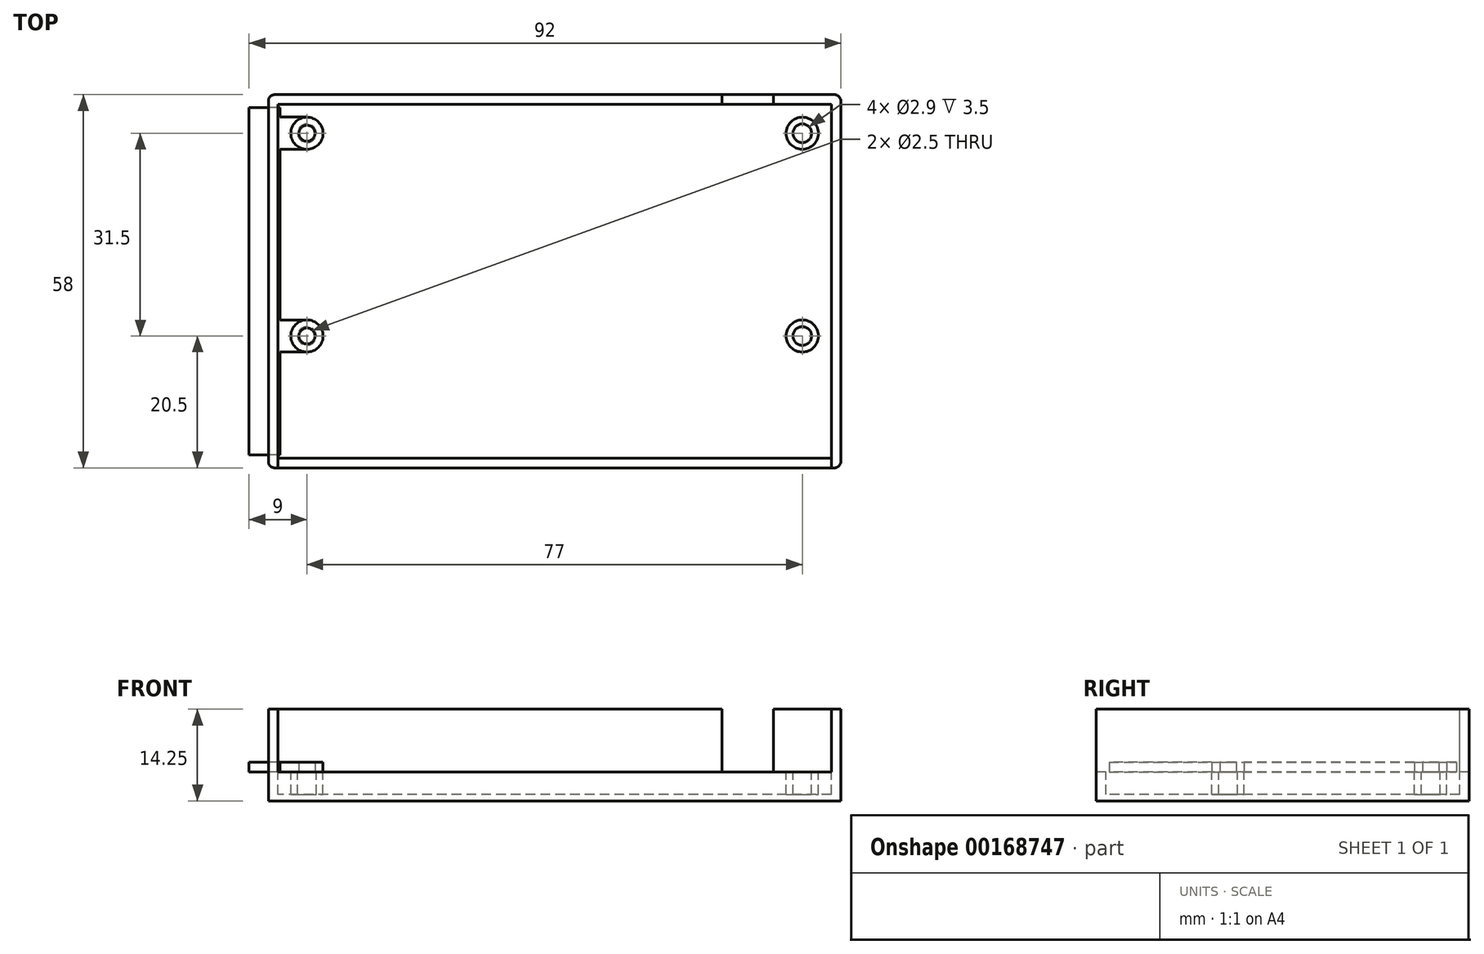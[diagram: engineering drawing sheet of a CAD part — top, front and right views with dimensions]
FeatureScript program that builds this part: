
annotation { "Feature Type Name" : "Feature", "Feature Type Description" : "" }
export const myFeature = defineFeature(function(context is Context, id is Id, definition is map)
    precondition{}
    {
        {
            var Q0;
            Q0=qCreatedBy(makeId("Top.planeOp"),FACE);
            var sketch = newSketch(context, id + "F11", { "sketchPlane" : qUnion([Q0])});
            skLineSegment(sketch, "E0.bottom", {"start": v(42.5, 27) * mm, "end": v(-42.5, 27) * mm});
            skLineSegment(sketch, "E0.top", {"start": v(42.5, -27) * mm, "end": v(-42.5, -27) * mm});
            skLineSegment(sketch, "E0.left", {"start": v(42.5, 27) * mm, "end": v(42.5, -27) * mm});
            skLineSegment(sketch, "E0.right", {"start": v(-42.5, 27) * mm, "end": v(-42.5, -27) * mm});
            skPoint(sketch, "E0.middle", {"position": v(0, 0) * mm});
            skCircle(sketch, "E1", {"center": v(-38.5, 23) * mm, "radius": 1.25 * mm, "construction": true});
            skCircle(sketch, "E2", {"center": v(38.5, 23) * mm, "radius": 1.25 * mm, "construction": true});
            skCircle(sketch, "E3", {"center": v(-38.5, -8.5) * mm, "radius": 1.25 * mm, "construction": true});
            skCircle(sketch, "E4", {"center": v(38.5, -8.5) * mm, "radius": 1.25 * mm, "construction": true});
            skPoint(sketch, "E5", {"position": v(-34.5, -27) * mm});
            skPoint(sketch, "E6", {"position": v(-17.5, -27) * mm});
            skPoint(sketch, "E7", {"position": v(-0.9, -27) * mm});
            skPoint(sketch, "E8", {"position": v(14.1, -27) * mm});
            skPoint(sketch, "E9", {"position": v(33.5, -27) * mm});
            skCircle(sketch, "E10", {"center": v(-38.5, 23) * mm, "radius": 2.5 * mm, "construction": true});
            skCircle(sketch, "E11", {"center": v(38.5, 23) * mm, "radius": 2.5 * mm, "construction": true});
            skCircle(sketch, "E12", {"center": v(38.5, -8.5) * mm, "radius": 2.5 * mm, "construction": true});
            skCircle(sketch, "E13", {"center": v(-38.5, -8.5) * mm, "radius": 2.5 * mm, "construction": true});
            skLineSegment(sketch, "E14.bottom", {"start": v(-41.5, -27) * mm, "end": v(-27.5, -27) * mm, "construction": true});
            skLineSegment(sketch, "E14.top", {"start": v(-41.5, -12) * mm, "end": v(-27.5, -12) * mm, "construction": true});
            skLineSegment(sketch, "E14.left", {"start": v(-41.5, -27) * mm, "end": v(-41.5, -12) * mm, "construction": true});
            skLineSegment(sketch, "E14.right", {"start": v(-27.5, -27) * mm, "end": v(-27.5, -12) * mm, "construction": true});
            skLineSegment(sketch, "E15.bottom", {"start": v(-25, -17) * mm, "end": v(-10, -17) * mm, "construction": true});
            skLineSegment(sketch, "E15.top", {"start": v(-25, -27) * mm, "end": v(-10, -27) * mm, "construction": true});
            skLineSegment(sketch, "E15.left", {"start": v(-25, -17) * mm, "end": v(-25, -27) * mm, "construction": true});
            skLineSegment(sketch, "E15.right", {"start": v(-10, -17) * mm, "end": v(-10, -27) * mm, "construction": true});
            skLineSegment(sketch, "E16.bottom", {"start": v(-4.9, -21) * mm, "end": v(3.1, -21) * mm, "construction": true});
            skLineSegment(sketch, "E16.top", {"start": v(-4.9, -27) * mm, "end": v(3.1, -27) * mm, "construction": true});
            skLineSegment(sketch, "E16.left", {"start": v(-4.9, -21) * mm, "end": v(-4.9, -27) * mm, "construction": true});
            skLineSegment(sketch, "E16.right", {"start": v(3.1, -21) * mm, "end": v(3.1, -27) * mm, "construction": true});
            skLineSegment(sketch, "E17.bottom", {"start": v(6.6, -13) * mm, "end": v(21.6, -13) * mm, "construction": true});
            skLineSegment(sketch, "E17.top", {"start": v(6.6, -27) * mm, "end": v(21.6, -27) * mm, "construction": true});
            skLineSegment(sketch, "E17.left", {"start": v(6.6, -13) * mm, "end": v(6.6, -27) * mm, "construction": true});
            skLineSegment(sketch, "E17.right", {"start": v(21.6, -13) * mm, "end": v(21.6, -27) * mm, "construction": true});
            skLineSegment(sketch, "E18.bottom", {"start": v(26, -13) * mm, "end": v(41, -13) * mm, "construction": true});
            skLineSegment(sketch, "E18.top", {"start": v(26, -27) * mm, "end": v(41, -27) * mm, "construction": true});
            skLineSegment(sketch, "E18.left", {"start": v(26, -13) * mm, "end": v(26, -27) * mm, "construction": true});
            skLineSegment(sketch, "E18.right", {"start": v(41, -13) * mm, "end": v(41, -27) * mm, "construction": true});
            skPoint(sketch, "E19", {"position": v(30, 27) * mm});
            skLineSegment(sketch, "E20.bottom", {"start": v(26, 27) * mm, "end": v(34, 27) * mm, "construction": true});
            skLineSegment(sketch, "E20.top", {"start": v(26, 14) * mm, "end": v(34, 14) * mm, "construction": true});
            skLineSegment(sketch, "E20.left", {"start": v(26, 27) * mm, "end": v(26, 14) * mm, "construction": true});
            skLineSegment(sketch, "E20.right", {"start": v(34, 27) * mm, "end": v(34, 14) * mm, "construction": true});
            skLineSegment(sketch, "E21.bottom", {"start": v(-31.5, 21) * mm, "end": v(-33.5, 21) * mm, "construction": true});
            skLineSegment(sketch, "E21.top", {"start": v(-31.5, 25) * mm, "end": v(-33.5, 25) * mm, "construction": true});
            skLineSegment(sketch, "E21.left", {"start": v(-31.5, 21) * mm, "end": v(-31.5, 25) * mm, "construction": true});
            skLineSegment(sketch, "E21.right", {"start": v(-33.5, 21) * mm, "end": v(-33.5, 25) * mm, "construction": true});
            skPoint(sketch, "E21.middle", {"position": v(-32.5, 23) * mm});
            skLineSegment(sketch, "E22", {"start": v(-32.5, 24) * mm, "end": v(-32.5, 22) * mm, "construction": true});
            skPoint(sketch, "E23.1.0.0", {"position": v(-30.5, 23) * mm});
            skLineSegment(sketch, "E23.1.0.2", {"start": v(-29.5, 21) * mm, "end": v(-29.5, 25) * mm, "construction": true});
            skLineSegment(sketch, "E23.1.0.3", {"start": v(-29.5, 25) * mm, "end": v(-31.5, 25) * mm, "construction": true});
            skLineSegment(sketch, "E23.1.0.4", {"start": v(-29.5, 21) * mm, "end": v(-31.5, 21) * mm, "construction": true});
            skLineSegment(sketch, "E23.1.0.5", {"start": v(-30.5, 24) * mm, "end": v(-30.5, 22) * mm, "construction": true});
            skPoint(sketch, "E23.2.0.0", {"position": v(-28.5, 23) * mm});
            skLineSegment(sketch, "E23.2.0.1", {"start": v(-29.5, 21) * mm, "end": v(-29.5, 25) * mm, "construction": true});
            skLineSegment(sketch, "E23.2.0.2", {"start": v(-27.5, 21) * mm, "end": v(-27.5, 25) * mm, "construction": true});
            skLineSegment(sketch, "E23.2.0.3", {"start": v(-27.5, 25) * mm, "end": v(-29.5, 25) * mm, "construction": true});
            skLineSegment(sketch, "E23.2.0.4", {"start": v(-27.5, 21) * mm, "end": v(-29.5, 21) * mm, "construction": true});
            skLineSegment(sketch, "E23.2.0.5", {"start": v(-28.5, 24) * mm, "end": v(-28.5, 22) * mm, "construction": true});
            skPoint(sketch, "E23.3.0.0", {"position": v(-26.5, 23) * mm});
            skLineSegment(sketch, "E23.3.0.1", {"start": v(-27.5, 21) * mm, "end": v(-27.5, 25) * mm, "construction": true});
            skLineSegment(sketch, "E23.3.0.2", {"start": v(-25.5, 21) * mm, "end": v(-25.5, 25) * mm, "construction": true});
            skLineSegment(sketch, "E23.3.0.3", {"start": v(-25.5, 25) * mm, "end": v(-27.5, 25) * mm, "construction": true});
            skLineSegment(sketch, "E23.3.0.4", {"start": v(-25.5, 21) * mm, "end": v(-27.5, 21) * mm, "construction": true});
            skLineSegment(sketch, "E23.3.0.5", {"start": v(-26.5, 24) * mm, "end": v(-26.5, 22) * mm, "construction": true});
            skPoint(sketch, "E23.4.0.0", {"position": v(-24.5, 23) * mm});
            skLineSegment(sketch, "E23.4.0.1", {"start": v(-25.5, 21) * mm, "end": v(-25.5, 25) * mm, "construction": true});
            skLineSegment(sketch, "E23.4.0.2", {"start": v(-23.5, 21) * mm, "end": v(-23.5, 25) * mm, "construction": true});
            skLineSegment(sketch, "E23.4.0.3", {"start": v(-23.5, 25) * mm, "end": v(-25.5, 25) * mm, "construction": true});
            skLineSegment(sketch, "E23.4.0.4", {"start": v(-23.5, 21) * mm, "end": v(-25.5, 21) * mm, "construction": true});
            skLineSegment(sketch, "E23.4.0.5", {"start": v(-24.5, 24) * mm, "end": v(-24.5, 22) * mm, "construction": true});
            skPoint(sketch, "E23.5.0.0", {"position": v(-22.5, 23) * mm});
            skLineSegment(sketch, "E23.5.0.1", {"start": v(-23.5, 21) * mm, "end": v(-23.5, 25) * mm, "construction": true});
            skLineSegment(sketch, "E23.5.0.2", {"start": v(-21.5, 21) * mm, "end": v(-21.5, 25) * mm, "construction": true});
            skLineSegment(sketch, "E23.5.0.3", {"start": v(-21.5, 25) * mm, "end": v(-23.5, 25) * mm, "construction": true});
            skLineSegment(sketch, "E23.5.0.4", {"start": v(-21.5, 21) * mm, "end": v(-23.5, 21) * mm, "construction": true});
            skLineSegment(sketch, "E23.5.0.5", {"start": v(-22.5, 24) * mm, "end": v(-22.5, 22) * mm, "construction": true});
            skPoint(sketch, "E23.6.0.0", {"position": v(-20.5, 23) * mm});
            skLineSegment(sketch, "E23.6.0.1", {"start": v(-21.5, 21) * mm, "end": v(-21.5, 25) * mm, "construction": true});
            skLineSegment(sketch, "E23.6.0.2", {"start": v(-19.5, 21) * mm, "end": v(-19.5, 25) * mm, "construction": true});
            skLineSegment(sketch, "E23.6.0.3", {"start": v(-19.5, 25) * mm, "end": v(-21.5, 25) * mm, "construction": true});
            skLineSegment(sketch, "E23.6.0.4", {"start": v(-19.5, 21) * mm, "end": v(-21.5, 21) * mm, "construction": true});
            skLineSegment(sketch, "E23.6.0.5", {"start": v(-20.5, 24) * mm, "end": v(-20.5, 22) * mm, "construction": true});
            skPoint(sketch, "E23.7.0.0", {"position": v(-18.5, 23) * mm});
            skLineSegment(sketch, "E23.7.0.1", {"start": v(-19.5, 21) * mm, "end": v(-19.5, 25) * mm, "construction": true});
            skLineSegment(sketch, "E23.7.0.2", {"start": v(-17.5, 21) * mm, "end": v(-17.5, 25) * mm, "construction": true});
            skLineSegment(sketch, "E23.7.0.3", {"start": v(-17.5, 25) * mm, "end": v(-19.5, 25) * mm, "construction": true});
            skLineSegment(sketch, "E23.7.0.4", {"start": v(-17.5, 21) * mm, "end": v(-19.5, 21) * mm, "construction": true});
            skLineSegment(sketch, "E23.7.0.5", {"start": v(-18.5, 24) * mm, "end": v(-18.5, 22) * mm, "construction": true});
            skPoint(sketch, "E23.8.0.0", {"position": v(-16.5, 23) * mm});
            skLineSegment(sketch, "E23.8.0.1", {"start": v(-17.5, 21) * mm, "end": v(-17.5, 25) * mm, "construction": true});
            skLineSegment(sketch, "E23.8.0.2", {"start": v(-15.5, 21) * mm, "end": v(-15.5, 25) * mm, "construction": true});
            skLineSegment(sketch, "E23.8.0.3", {"start": v(-15.5, 25) * mm, "end": v(-17.5, 25) * mm, "construction": true});
            skLineSegment(sketch, "E23.8.0.4", {"start": v(-15.5, 21) * mm, "end": v(-17.5, 21) * mm, "construction": true});
            skLineSegment(sketch, "E23.8.0.5", {"start": v(-16.5, 24) * mm, "end": v(-16.5, 22) * mm, "construction": true});
            skPoint(sketch, "E23.9.0.0", {"position": v(-14.5, 23) * mm});
            skLineSegment(sketch, "E23.9.0.1", {"start": v(-15.5, 21) * mm, "end": v(-15.5, 25) * mm, "construction": true});
            skLineSegment(sketch, "E23.9.0.2", {"start": v(-13.5, 21) * mm, "end": v(-13.5, 25) * mm, "construction": true});
            skLineSegment(sketch, "E23.9.0.3", {"start": v(-13.5, 25) * mm, "end": v(-15.5, 25) * mm, "construction": true});
            skLineSegment(sketch, "E23.9.0.4", {"start": v(-13.5, 21) * mm, "end": v(-15.5, 21) * mm, "construction": true});
            skLineSegment(sketch, "E23.9.0.5", {"start": v(-14.5, 24) * mm, "end": v(-14.5, 22) * mm, "construction": true});
            skPoint(sketch, "E23.10.0.0", {"position": v(-12.5, 23) * mm});
            skLineSegment(sketch, "E23.10.0.1", {"start": v(-13.5, 21) * mm, "end": v(-13.5, 25) * mm, "construction": true});
            skLineSegment(sketch, "E23.10.0.2", {"start": v(-11.5, 21) * mm, "end": v(-11.5, 25) * mm, "construction": true});
            skLineSegment(sketch, "E23.10.0.3", {"start": v(-11.5, 25) * mm, "end": v(-13.5, 25) * mm, "construction": true});
            skLineSegment(sketch, "E23.10.0.4", {"start": v(-11.5, 21) * mm, "end": v(-13.5, 21) * mm, "construction": true});
            skLineSegment(sketch, "E23.10.0.5", {"start": v(-12.5, 24) * mm, "end": v(-12.5, 22) * mm, "construction": true});
            skPoint(sketch, "E23.11.0.0", {"position": v(-10.5, 23) * mm});
            skLineSegment(sketch, "E23.11.0.1", {"start": v(-11.5, 21) * mm, "end": v(-11.5, 25) * mm, "construction": true});
            skLineSegment(sketch, "E23.11.0.2", {"start": v(-9.5, 21) * mm, "end": v(-9.5, 25) * mm, "construction": true});
            skLineSegment(sketch, "E23.11.0.3", {"start": v(-9.5, 25) * mm, "end": v(-11.5, 25) * mm, "construction": true});
            skLineSegment(sketch, "E23.11.0.4", {"start": v(-9.5, 21) * mm, "end": v(-11.5, 21) * mm, "construction": true});
            skLineSegment(sketch, "E23.11.0.5", {"start": v(-10.5, 24) * mm, "end": v(-10.5, 22) * mm, "construction": true});
            skPoint(sketch, "E23.12.0.0", {"position": v(-8.5, 23) * mm});
            skLineSegment(sketch, "E23.12.0.1", {"start": v(-9.5, 21) * mm, "end": v(-9.5, 25) * mm, "construction": true});
            skLineSegment(sketch, "E23.12.0.2", {"start": v(-7.5, 21) * mm, "end": v(-7.5, 25) * mm, "construction": true});
            skLineSegment(sketch, "E23.12.0.3", {"start": v(-7.5, 25) * mm, "end": v(-9.5, 25) * mm, "construction": true});
            skLineSegment(sketch, "E23.12.0.4", {"start": v(-7.5, 21) * mm, "end": v(-9.5, 21) * mm, "construction": true});
            skLineSegment(sketch, "E23.12.0.5", {"start": v(-8.5, 24) * mm, "end": v(-8.5, 22) * mm, "construction": true});
            skPoint(sketch, "E23.13.0.0", {"position": v(-6.5, 23) * mm});
            skLineSegment(sketch, "E23.13.0.1", {"start": v(-7.5, 21) * mm, "end": v(-7.5, 25) * mm, "construction": true});
            skLineSegment(sketch, "E23.13.0.2", {"start": v(-5.5, 21) * mm, "end": v(-5.5, 25) * mm, "construction": true});
            skLineSegment(sketch, "E23.13.0.3", {"start": v(-5.5, 25) * mm, "end": v(-7.5, 25) * mm, "construction": true});
            skLineSegment(sketch, "E23.13.0.4", {"start": v(-5.5, 21) * mm, "end": v(-7.5, 21) * mm, "construction": true});
            skLineSegment(sketch, "E23.13.0.5", {"start": v(-6.5, 24) * mm, "end": v(-6.5, 22) * mm, "construction": true});
            skPoint(sketch, "E23.14.0.0", {"position": v(-4.5, 23) * mm});
            skLineSegment(sketch, "E23.14.0.1", {"start": v(-5.5, 21) * mm, "end": v(-5.5, 25) * mm, "construction": true});
            skLineSegment(sketch, "E23.14.0.2", {"start": v(-3.5, 21) * mm, "end": v(-3.5, 25) * mm, "construction": true});
            skLineSegment(sketch, "E23.14.0.3", {"start": v(-3.5, 25) * mm, "end": v(-5.5, 25) * mm, "construction": true});
            skLineSegment(sketch, "E23.14.0.4", {"start": v(-3.5, 21) * mm, "end": v(-5.5, 21) * mm, "construction": true});
            skLineSegment(sketch, "E23.14.0.5", {"start": v(-4.5, 24) * mm, "end": v(-4.5, 22) * mm, "construction": true});
            skPoint(sketch, "E23.15.0.0", {"position": v(-2.5, 23) * mm});
            skLineSegment(sketch, "E23.15.0.1", {"start": v(-3.5, 21) * mm, "end": v(-3.5, 25) * mm, "construction": true});
            skLineSegment(sketch, "E23.15.0.2", {"start": v(-1.5, 21) * mm, "end": v(-1.5, 25) * mm, "construction": true});
            skLineSegment(sketch, "E23.15.0.3", {"start": v(-1.5, 25) * mm, "end": v(-3.5, 25) * mm, "construction": true});
            skLineSegment(sketch, "E23.15.0.4", {"start": v(-1.5, 21) * mm, "end": v(-3.5, 21) * mm, "construction": true});
            skLineSegment(sketch, "E23.15.0.5", {"start": v(-2.5, 24) * mm, "end": v(-2.5, 22) * mm, "construction": true});
            skPoint(sketch, "E23.16.0.0", {"position": v(-0.5, 23) * mm});
            skLineSegment(sketch, "E23.16.0.1", {"start": v(-1.5, 21) * mm, "end": v(-1.5, 25) * mm, "construction": true});
            skLineSegment(sketch, "E23.16.0.2", {"start": v(0.5, 21) * mm, "end": v(0.5, 25) * mm, "construction": true});
            skLineSegment(sketch, "E23.16.0.3", {"start": v(0.5, 25) * mm, "end": v(-1.5, 25) * mm, "construction": true});
            skLineSegment(sketch, "E23.16.0.4", {"start": v(0.5, 21) * mm, "end": v(-1.5, 21) * mm, "construction": true});
            skLineSegment(sketch, "E23.16.0.5", {"start": v(-0.5, 24) * mm, "end": v(-0.5, 22) * mm, "construction": true});
            skPoint(sketch, "E23.17.0.0", {"position": v(1.5, 23) * mm});
            skLineSegment(sketch, "E23.17.0.1", {"start": v(0.5, 21) * mm, "end": v(0.5, 25) * mm, "construction": true});
            skLineSegment(sketch, "E23.17.0.2", {"start": v(2.5, 21) * mm, "end": v(2.5, 25) * mm, "construction": true});
            skLineSegment(sketch, "E23.17.0.3", {"start": v(2.5, 25) * mm, "end": v(0.5, 25) * mm, "construction": true});
            skLineSegment(sketch, "E23.17.0.4", {"start": v(2.5, 21) * mm, "end": v(0.5, 21) * mm, "construction": true});
            skLineSegment(sketch, "E23.17.0.5", {"start": v(1.5, 24) * mm, "end": v(1.5, 22) * mm, "construction": true});
            skPoint(sketch, "E23.18.0.0", {"position": v(3.5, 23) * mm});
            skLineSegment(sketch, "E23.18.0.1", {"start": v(2.5, 21) * mm, "end": v(2.5, 25) * mm, "construction": true});
            skLineSegment(sketch, "E23.18.0.2", {"start": v(4.5, 21) * mm, "end": v(4.5, 25) * mm, "construction": true});
            skLineSegment(sketch, "E23.18.0.3", {"start": v(4.5, 25) * mm, "end": v(2.5, 25) * mm, "construction": true});
            skLineSegment(sketch, "E23.18.0.4", {"start": v(4.5, 21) * mm, "end": v(2.5, 21) * mm, "construction": true});
            skLineSegment(sketch, "E23.18.0.5", {"start": v(3.5, 24) * mm, "end": v(3.5, 22) * mm, "construction": true});
            skPoint(sketch, "E23.19.0.0", {"position": v(5.5, 23) * mm});
            skLineSegment(sketch, "E23.19.0.1", {"start": v(4.5, 21) * mm, "end": v(4.5, 25) * mm, "construction": true});
            skLineSegment(sketch, "E23.19.0.2", {"start": v(6.5, 21) * mm, "end": v(6.5, 25) * mm, "construction": true});
            skLineSegment(sketch, "E23.19.0.3", {"start": v(6.5, 25) * mm, "end": v(4.5, 25) * mm, "construction": true});
            skLineSegment(sketch, "E23.19.0.4", {"start": v(6.5, 21) * mm, "end": v(4.5, 21) * mm, "construction": true});
            skLineSegment(sketch, "E23.19.0.5", {"start": v(5.5, 24) * mm, "end": v(5.5, 22) * mm, "construction": true});
            skLineSegment(sketch, "E23.direction1", {"start": v(-33.5, 21) * mm, "end": v(-31.5, 21) * mm, "construction": true});
            skLineSegment(sketch, "E24.bottom", {"start": v(8, 19.75) * mm, "end": v(-35, 19.75) * mm, "construction": true});
            skLineSegment(sketch, "E24.top", {"start": v(8, 26.25) * mm, "end": v(-35, 26.25) * mm, "construction": true});
            skLineSegment(sketch, "E24.left", {"start": v(8, 19.75) * mm, "end": v(8, 26.25) * mm, "construction": true});
            skLineSegment(sketch, "E24.right", {"start": v(-35, 19.75) * mm, "end": v(-35, 26.25) * mm, "construction": true});
            skPoint(sketch, "E24.middle", {"position": v(-13.5, 23) * mm});
            skSolve(sketch);
        }
        {
            var Q0;
            Q0=qCreatedBy(makeId("Front.planeOp"),FACE);
            var sketch = newSketch(context, id + "F0", { "sketchPlane" : qUnion([Q0])});
            skLineSegment(sketch, "E25", {"start": v(0, 0) * mm, "end": v(0, -3.5) * mm});
            skLineSegment(sketch, "E26", {"start": v(0, 0) * mm, "end": v(0, 1.25) * mm});
            skLineSegment(sketch, "E27", {"start": v(0, 1.25) * mm, "end": v(0, 9.75) * mm});
            skSolve(sketch);
        }
        {
            var Q0;
            Q0=sQuery(id+"F0.wireOp",VERTEX,"E25.end");
            var Q1;
            Q1=sQuery(id+"F0.wireOp",EDGE,"E25");
            cPlane(context, id + "F1", {"entities" : qUnion([Q0, Q1]), "cplaneType" : CPlaneType.LINE_POINT, "offset" : 25 * mm, "width" : 150 * mm, "height" : 150 * mm});
        }
        {
            var Q0;
            Q0=qCreatedBy(id+"F1.planeOp",FACE);
            var sketch = newSketch(context, id + "F2", { "sketchPlane" : qUnion([Q0])});
            skLineSegment(sketch, "E28.0", {"start": v(43, -27.5) * mm, "end": v(-43, -27.5) * mm});
            skLineSegment(sketch, "E28.1", {"start": v(43, -27.5) * mm, "end": v(43, 27.5) * mm});
            skLineSegment(sketch, "E28.2", {"start": v(43, 27.5) * mm, "end": v(-43, 27.5) * mm});
            skLineSegment(sketch, "E28.3", {"start": v(-43, -27.5) * mm, "end": v(-43, 27.5) * mm});
            skLineSegment(sketch, "E29.bottom", {"start": v(44.5, -29) * mm, "end": v(-44.5, -29) * mm});
            skLineSegment(sketch, "E29.top", {"start": v(44.5, 29) * mm, "end": v(-44.5, 29) * mm});
            skLineSegment(sketch, "E29.left", {"start": v(44.5, -29) * mm, "end": v(44.5, 29) * mm});
            skLineSegment(sketch, "E29.right", {"start": v(-44.5, -29) * mm, "end": v(-44.5, 29) * mm});
            skPoint(sketch, "E29.middle", {"position": v(0, 0) * mm});
            skLineSegment(sketch, "E30", {"start": v(-43, 27.5) * mm, "end": v(-43, 29) * mm});
            skLineSegment(sketch, "E31", {"start": v(43, 27.5) * mm, "end": v(43, 29) * mm});
            skLineSegment(sketch, "E32.0", {"start": v(26, -27) * mm, "end": v(34, -27) * mm, "construction": true});
            skLineSegment(sketch, "E33", {"start": v(26, -29) * mm, "end": v(26, -27.5) * mm});
            skLineSegment(sketch, "E34", {"start": v(34, -29) * mm, "end": v(34, -27.5) * mm});
            skSolve(sketch);
        }
        {
            var Q0;
            Q0=makeQuery(id+"F2.imprint","IMPRINT",FACE,{"disambiguationData":[TD([[makeQuery(id+"F2.imprint","IMPRINT",EDGE,{"derivedFrom":sQuery(id+"F2.wireOp",EDGE,"E28.0")}),-1.0]])]});
            var Q1;
            Q1=makeQuery(id+"F2.imprint","IMPRINT",FACE,{"disambiguationData":[TD([[makeQuery(id+"F2.imprint","IMPRINT",EDGE,{"derivedFrom":sQuery(id+"F2.wireOp",EDGE,"E28.2")}),-1.0]])]});
            var Q2;
            {var subQ5=sQuery(id+"F2.wireOp",EDGE,"E28.3");Q2=makeQuery(id+"F2.imprint","IMPRINT",FACE,{"disambiguationData":[TD([[makeQuery(id+"F2.imprint","IMPRINT",EDGE,{"derivedFrom":subQ5}),1.0]])]});}
            var Q3;
            {var subQ0=sQuery(id+"F2.wireOp",EDGE,"E33");Q3=makeQuery(id+"F2.imprint","IMPRINT",FACE,{"disambiguationData":[TD([[makeQuery(id+"F2.imprint","IMPRINT",EDGE,{"derivedFrom":subQ0}),-1.0]])]});}
            var Q4;
            {var subQ5=sQuery(id+"F2.wireOp",EDGE,"E28.1");Q4=makeQuery(id+"F2.imprint","IMPRINT",FACE,{"disambiguationData":[TD([[makeQuery(id+"F2.imprint","IMPRINT",EDGE,{"derivedFrom":subQ5}),-1.0]])]});}
            extrude(context, id + "F3", {"entities" : qUnion([Q0, Q1, Q2, Q3, Q4]), "depth" : 1 * mm});
        }
        {
            var Q0;
            {var subQ5=sQuery(id+"F2.wireOp",EDGE,"E28.3");Q0=makeQuery(id+"F2.imprint","IMPRINT",FACE,{"disambiguationData":[TD([[makeQuery(id+"F2.imprint","IMPRINT",EDGE,{"derivedFrom":subQ5}),1.0]])]});}
            var Q1;
            {var subQ5=sQuery(id+"F2.wireOp",EDGE,"E28.1");Q1=makeQuery(id+"F2.imprint","IMPRINT",FACE,{"disambiguationData":[TD([[makeQuery(id+"F2.imprint","IMPRINT",EDGE,{"derivedFrom":subQ5}),-1.0]])]});}
            var Q2;
            Q2=sQuery(id+"F0.wireOp",EDGE,"E25");
            var Q3;
            Q3=sQuery(id+"F0.wireOp",EDGE,"E26");
            var Q4;
            Q4=sQuery(id+"F0.wireOp",EDGE,"E27");
            sweep(context, id + "F4", {"operationType" : NewBodyOperationType.ADD, "profiles" : qUnion([Q0, Q1]), "path" : qUnion([Q2, Q3, Q4])});
        }
        {
            var Q0;
            Q0=qCreatedBy(id+"F1.planeOp",FACE);
            var sketch = newSketch(context, id + "F5", { "sketchPlane" : qUnion([Q0])});
            skCircle(sketch, "E35.0", {"center": v(-38.5, -23) * mm, "radius": 2.5 * mm});
            skCircle(sketch, "E36.0", {"center": v(-38.5, -23) * mm, "radius": 1.25 * mm, "construction": true});
            skCircle(sketch, "E37.0", {"center": v(-38.5, 8.5) * mm, "radius": 2.5 * mm});
            skCircle(sketch, "E38.0", {"center": v(-38.5, 8.5) * mm, "radius": 1.25 * mm, "construction": true});
            skCircle(sketch, "E39.0", {"center": v(38.5, 8.5) * mm, "radius": 2.5 * mm});
            skCircle(sketch, "E40.0", {"center": v(38.5, 8.5) * mm, "radius": 1.25 * mm, "construction": true});
            skCircle(sketch, "E41.0", {"center": v(38.5, -23) * mm, "radius": 2.5 * mm});
            skCircle(sketch, "E42.0", {"center": v(38.5, -23) * mm, "radius": 1.25 * mm, "construction": true});
            skCircle(sketch, "E43.0", {"center": v(-38.5, -23) * mm, "radius": 1.45 * mm});
            skCircle(sketch, "E44", {"center": v(38.5, -23) * mm, "radius": 1.45 * mm});
            skCircle(sketch, "E45", {"center": v(-38.5, 8.5) * mm, "radius": 1.45 * mm});
            skCircle(sketch, "E46", {"center": v(38.5, 8.5) * mm, "radius": 1.45 * mm});
            skSolve(sketch);
        }
        {
            var Q0;
            Q0 = qSketchRegion(id + "F5", true);
            var Q1;
            Q1=sQuery(id+"F0.wireOp",EDGE,"E25");
            sweep(context, id + "F6", {"operationType" : NewBodyOperationType.ADD, "profiles" : qUnion([Q0]), "path" : qUnion([Q1])});
        }
        {
            var Q0;
            Q0=makeQuery(id+"F2.imprint","IMPRINT",FACE,{"disambiguationData":[TD([[makeQuery(id+"F2.imprint","IMPRINT",EDGE,{"derivedFrom":sQuery(id+"F2.wireOp",EDGE,"E28.2")}),-1.0]])]});
            var Q1;
            {var subQ0=sQuery(id+"F2.wireOp",EDGE,"E33");Q1=makeQuery(id+"F2.imprint","IMPRINT",FACE,{"disambiguationData":[TD([[makeQuery(id+"F2.imprint","IMPRINT",EDGE,{"derivedFrom":subQ0}),-1.0]])]});}
            var Q2;
            Q2=sQuery(id+"F0.wireOp",EDGE,"E25");
            sweep(context, id + "F7", {"operationType" : NewBodyOperationType.ADD, "profiles" : qUnion([Q0, Q1]), "path" : qUnion([Q2])});
        }
        {
            var Q0;
            {var subQ0=sQuery(id+"F2.wireOp",EDGE,"E29.left");var subQ1=sQuery(id+"F2.wireOp",EDGE,"E29.top");Q0=makeQuery(id+"F4.boolean.opBoolean","MERGE",EDGE,{"derivedFrom":[makeQuery(id+"F3.opExtrude","SWEPT_EDGE",EDGE,{"disambiguationData":[OSD([subQ1,subQ0])]}),makeQuery(id+"F4.opSweep","SWEPT_EDGE",EDGE,{"disambiguationData":[OSD([sQuery(id+"F0.wireOp",EDGE,"E25"),subQ1,subQ0])]})]});}
            var Q1;
            {var subQ0=sQuery(id+"F2.wireOp",EDGE,"E29.left");var subQ1=sQuery(id+"F2.wireOp",EDGE,"E29.bottom");Q1=makeQuery(id+"F4.boolean.opBoolean","MERGE",EDGE,{"derivedFrom":[makeQuery(id+"F3.opExtrude","SWEPT_EDGE",EDGE,{"disambiguationData":[OSD([subQ1,subQ0])]}),makeQuery(id+"F4.opSweep","SWEPT_EDGE",EDGE,{"disambiguationData":[OSD([sQuery(id+"F0.wireOp",EDGE,"E25"),subQ1,subQ0])]})]});}
            var Q2;
            {var subQ0=sQuery(id+"F2.wireOp",EDGE,"E29.right");var subQ1=sQuery(id+"F2.wireOp",EDGE,"E29.top");Q2=makeQuery(id+"F4.boolean.opBoolean","MERGE",EDGE,{"derivedFrom":[makeQuery(id+"F3.opExtrude","SWEPT_EDGE",EDGE,{"disambiguationData":[OSD([subQ1,subQ0])]}),makeQuery(id+"F4.opSweep","SWEPT_EDGE",EDGE,{"disambiguationData":[OSD([sQuery(id+"F0.wireOp",EDGE,"E25"),subQ1,subQ0])]})]});}
            var Q3;
            {var subQ0=sQuery(id+"F2.wireOp",EDGE,"E29.right");var subQ1=sQuery(id+"F2.wireOp",EDGE,"E29.bottom");Q3=makeQuery(id+"F4.boolean.opBoolean","MERGE",EDGE,{"derivedFrom":[makeQuery(id+"F3.opExtrude","SWEPT_EDGE",EDGE,{"disambiguationData":[OSD([subQ1,subQ0])]}),makeQuery(id+"F4.opSweep","SWEPT_EDGE",EDGE,{"disambiguationData":[OSD([sQuery(id+"F0.wireOp",EDGE,"E25"),subQ1,subQ0])]})]});}
            fillet(context, id + "F8", {"entities" : qUnion([Q0, Q1, Q2, Q3]), "radius" : 1 * mm, "allowEdgeOverflow" : false});
        }
        {
            var Q0;
            Q0=qCreatedBy(makeId("Top.planeOp"),FACE);
            var sketch = newSketch(context, id + "F9", { "sketchPlane" : qUnion([Q0])});
            skLineSegment(sketch, "E47.0.0", {"start": v(42.5, -27) * mm, "end": v(42.5, 27) * mm, "construction": true});
            skLineSegment(sketch, "E47.0.1", {"start": v(42.5, 27) * mm, "end": v(-42.5, 27) * mm, "construction": true});
            skLineSegment(sketch, "E47.0.2", {"start": v(-42.5, 27) * mm, "end": v(-42.5, -27) * mm, "construction": true});
            skLineSegment(sketch, "E47.0.3", {"start": v(-42.5, -27) * mm, "end": v(42.5, -27) * mm, "construction": true});
            skCircle(sketch, "E48.0", {"center": v(-38.5, 23) * mm, "radius": 1.25 * mm});
            skCircle(sketch, "E49.0", {"center": v(-38.5, -8.5) * mm, "radius": 1.25 * mm});
            skLineSegment(sketch, "E50.0", {"start": v(-42.7, 27) * mm, "end": v(-42.7, -27) * mm});
            skLineSegment(sketch, "E51.bottom", {"start": v(47.5, 27) * mm, "end": v(-47.5, 27) * mm, "construction": true});
            skLineSegment(sketch, "E51.top", {"start": v(47.5, -27) * mm, "end": v(-47.5, -27) * mm, "construction": true});
            skLineSegment(sketch, "E51.left", {"start": v(47.5, 27) * mm, "end": v(47.5, -27) * mm, "construction": true});
            skLineSegment(sketch, "E51.right", {"start": v(-47.5, 27) * mm, "end": v(-47.5, -27) * mm, "construction": true});
            skPoint(sketch, "E51.middle", {"position": v(0, 0) * mm});
            skLineSegment(sketch, "E52", {"start": v(-42.7, 27) * mm, "end": v(-47.5, 27) * mm});
            skLineSegment(sketch, "E53", {"start": v(-47.5, -27) * mm, "end": v(-47.5, 27) * mm});
            skLineSegment(sketch, "E54", {"start": v(-42.7, -27) * mm, "end": v(-47.5, -27) * mm});
            skArc(sketch, "E55", {"start": v(-38.5, 25.5) * mm, "mid": v(-36, 23) * mm, "end": v(-38.5, 20.5) * mm});
            skLineSegment(sketch, "E56", {"start": v(-38.5, 25.5) * mm, "end": v(-42.7, 25.5) * mm});
            skLineSegment(sketch, "E57", {"start": v(-38.5, 20.5) * mm, "end": v(-42.7, 20.5) * mm});
            skArc(sketch, "E58", {"start": v(-38.5, -6) * mm, "mid": v(-36, -8.5) * mm, "end": v(-38.5, -11) * mm});
            skLineSegment(sketch, "E59", {"start": v(-38.5, -6) * mm, "end": v(-42.7, -6) * mm});
            skLineSegment(sketch, "E60", {"start": v(-38.5, -11) * mm, "end": v(-42.7, -11) * mm});
            skSolve(sketch);
        }
        {
            var Q0;
            Q0 = qSketchRegion(id + "F9", true);
            extrude(context, id + "F10", {"entities" : qUnion([Q0]), "depth" : 1.5 * mm});
        }
    });
